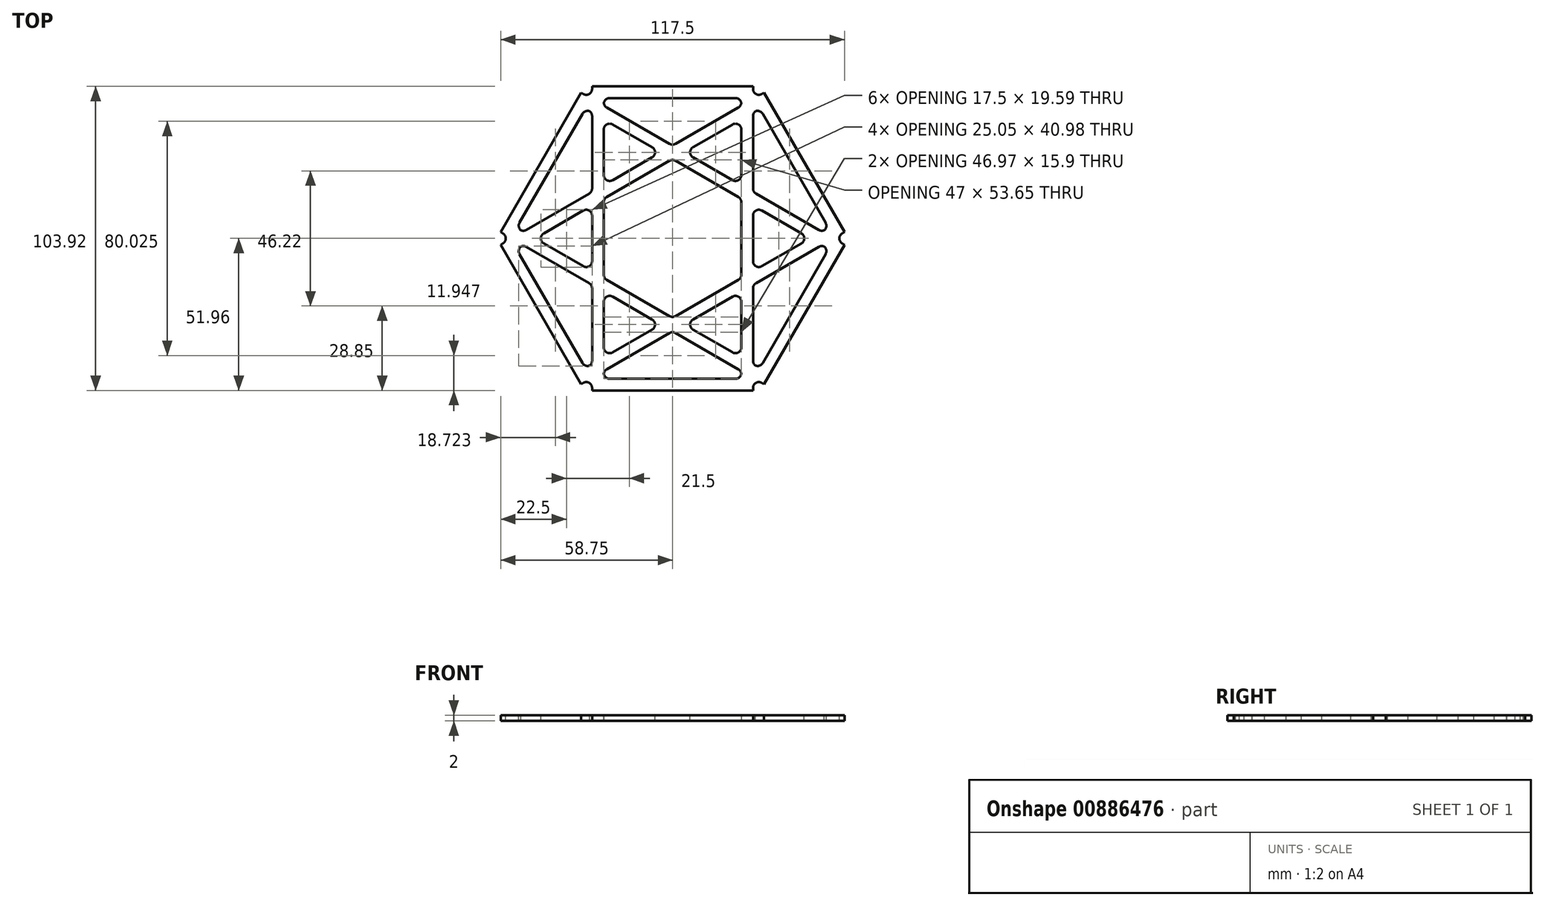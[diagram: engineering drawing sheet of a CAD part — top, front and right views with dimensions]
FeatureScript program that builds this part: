
annotation { "Feature Type Name" : "Feature", "Feature Type Description" : "" }
export const myFeature = defineFeature(function(context is Context, id is Id, definition is map)
    precondition{}
    {
        {
            var Q0;
            Q0=qCreatedBy(makeId("Top.planeOp"),FACE);
            var sketch = newSketch(context, id + "F0", { "sketchPlane" : qUnion([Q0])});
            skCircle(sketch, "E0.cCircle", {"center": v(0, 0) * mm, "radius": 60 * mm, "construction": true});
            skLineSegment(sketch, "E0.0", {"start": v(-60, 0) * mm, "end": v(-30, 51.96) * mm, "construction": true});
            skLineSegment(sketch, "E0.1", {"start": v(-30, 51.96) * mm, "end": v(30, 51.96) * mm, "construction": true});
            skLineSegment(sketch, "E0.2", {"start": v(30, 51.96) * mm, "end": v(60, 0) * mm, "construction": true});
            skLineSegment(sketch, "E0.3", {"start": v(60, 0) * mm, "end": v(30, -51.96) * mm, "construction": true});
            skLineSegment(sketch, "E0.4", {"start": v(30, -51.96) * mm, "end": v(-30, -51.96) * mm, "construction": true});
            skLineSegment(sketch, "E0.5", {"start": v(-30, -51.96) * mm, "end": v(-60, 0) * mm, "construction": true});
            skLineSegment(sketch, "E1.bottom", {"start": v(-27.5, 51.96) * mm, "end": v(27.5, 51.96) * mm});
            skLineSegment(sketch, "E1.top", {"start": v(-27.5, -51.96) * mm, "end": v(27.5, -51.96) * mm});
            skLineSegment(sketch, "E1.left", {"start": v(-27.5, 51.96) * mm, "end": v(-27.5, -51.96) * mm});
            skLineSegment(sketch, "E1.right", {"start": v(27.5, 51.96) * mm, "end": v(27.5, -51.96) * mm});
            skLineSegment(sketch, "E2.0", {"start": v(-23.5, -47.96) * mm, "end": v(23.5, -47.96) * mm});
            skLineSegment(sketch, "E2.1", {"start": v(-23.5, 47.96) * mm, "end": v(-23.5, -47.96) * mm});
            skLineSegment(sketch, "E2.2", {"start": v(-23.5, 47.96) * mm, "end": v(23.5, 47.96) * mm});
            skLineSegment(sketch, "E2.3", {"start": v(23.5, 47.96) * mm, "end": v(23.5, -47.96) * mm});
            skLineSegment(sketch, "E3.1.0", {"start": v(-29.79, -44.33) * mm, "end": v(53.29, 3.63) * mm});
            skLineSegment(sketch, "E3.1.1", {"start": v(58.75, 2.17) * mm, "end": v(31.25, 49.8) * mm});
            skLineSegment(sketch, "E3.1.2", {"start": v(-31.25, -49.8) * mm, "end": v(-58.75, -2.17) * mm});
            skLineSegment(sketch, "E3.1.3", {"start": v(-29.79, -44.33) * mm, "end": v(-53.29, -3.63) * mm});
            skLineSegment(sketch, "E3.1.4", {"start": v(-53.29, -3.63) * mm, "end": v(29.79, 44.33) * mm});
            skLineSegment(sketch, "E3.1.5", {"start": v(-58.75, -2.17) * mm, "end": v(31.25, 49.8) * mm});
            skLineSegment(sketch, "E3.1.7", {"start": v(53.29, 3.63) * mm, "end": v(29.79, 44.33) * mm});
            skLineSegment(sketch, "E3.1.8", {"start": v(-31.25, -49.8) * mm, "end": v(58.75, 2.17) * mm});
            skLineSegment(sketch, "E3.2.0", {"start": v(53.29, -3.63) * mm, "end": v(-29.79, 44.33) * mm});
            skLineSegment(sketch, "E3.2.1", {"start": v(-31.25, 49.8) * mm, "end": v(-58.75, 2.17) * mm});
            skLineSegment(sketch, "E3.2.2", {"start": v(58.75, -2.17) * mm, "end": v(31.25, -49.8) * mm});
            skLineSegment(sketch, "E3.2.3", {"start": v(53.29, -3.63) * mm, "end": v(29.79, -44.33) * mm});
            skLineSegment(sketch, "E3.2.4", {"start": v(29.79, -44.33) * mm, "end": v(-53.29, 3.63) * mm});
            skLineSegment(sketch, "E3.2.5", {"start": v(31.25, -49.8) * mm, "end": v(-58.75, 2.17) * mm});
            skLineSegment(sketch, "E3.2.7", {"start": v(-29.79, 44.33) * mm, "end": v(-53.29, 3.63) * mm});
            skLineSegment(sketch, "E3.2.8", {"start": v(58.75, -2.17) * mm, "end": v(-31.25, 49.8) * mm});
            skSolve(sketch);
        }
        {
            var Q0;
            {var subQ0=sQuery(id+"F0.wireOp",EDGE,"E3.1.4");var subQ1=sQuery(id+"F0.wireOp",EDGE,"E1.left");var subQ2=makeQuery(id+"F0.imprint","INTERSECT",VERTEX,{"derivedFrom":[subQ1,subQ0]});Q0=makeQuery(id+"F0.imprint","IMPRINT",FACE,{"disambiguationData":[TD([[makeQuery(id+"F0.imprint","IMPRINT",EDGE,{"disambiguationData":[TD([[subQ2,-1.0]])],"derivedFrom":subQ1}),1.0]])]});}
            var Q1;
            {var subQ0=sQuery(id+"F0.wireOp",EDGE,"E3.2.4");var subQ1=sQuery(id+"F0.wireOp",EDGE,"E1.left");var subQ2=makeQuery(id+"F0.imprint","INTERSECT",VERTEX,{"derivedFrom":[subQ1,subQ0]});Q1=makeQuery(id+"F0.imprint","IMPRINT",FACE,{"disambiguationData":[TD([[makeQuery(id+"F0.imprint","IMPRINT",EDGE,{"disambiguationData":[TD([[subQ2,-1.0]])],"derivedFrom":subQ1}),1.0]])]});}
            var Q2;
            {var subQ0=sQuery(id+"F0.wireOp",EDGE,"E3.2.4");var subQ1=sQuery(id+"F0.wireOp",EDGE,"E2.1");var subQ2=makeQuery(id+"F0.imprint","INTERSECT",VERTEX,{"derivedFrom":[subQ1,subQ0]});Q2=makeQuery(id+"F0.imprint","IMPRINT",FACE,{"disambiguationData":[TD([[makeQuery(id+"F0.imprint","IMPRINT",EDGE,{"disambiguationData":[TD([[subQ2,-1.0]])],"derivedFrom":subQ1}),1.0]])]});}
            var Q3;
            {var subQ0=sQuery(id+"F0.wireOp",EDGE,"E3.2.4");var subQ1=sQuery(id+"F0.wireOp",EDGE,"E1.left");var subQ2=makeQuery(id+"F0.imprint","INTERSECT",VERTEX,{"derivedFrom":[subQ1,subQ0]});Q3=makeQuery(id+"F0.imprint","IMPRINT",FACE,{"disambiguationData":[TD([[makeQuery(id+"F0.imprint","IMPRINT",EDGE,{"disambiguationData":[TD([[subQ2,-1.0]])],"derivedFrom":subQ1}),-1.0]])]});}
            var Q4;
            {var subQ0=sQuery(id+"F0.wireOp",EDGE,"E3.2.5");var subQ1=sQuery(id+"F0.wireOp",EDGE,"E1.left");var subQ2=makeQuery(id+"F0.imprint","INTERSECT",VERTEX,{"derivedFrom":[subQ1,subQ0]});Q4=makeQuery(id+"F0.imprint","IMPRINT",FACE,{"disambiguationData":[TD([[makeQuery(id+"F0.imprint","IMPRINT",EDGE,{"disambiguationData":[TD([[subQ2,-1.0]])],"derivedFrom":subQ1}),1.0]])]});}
            var Q5;
            {var subQ0=sQuery(id+"F0.wireOp",EDGE,"E3.1.8");var subQ1=sQuery(id+"F0.wireOp",EDGE,"E1.left");var subQ2=makeQuery(id+"F0.imprint","INTERSECT",VERTEX,{"derivedFrom":[subQ1,subQ0]});Q5=makeQuery(id+"F0.imprint","IMPRINT",FACE,{"disambiguationData":[TD([[makeQuery(id+"F0.imprint","IMPRINT",EDGE,{"disambiguationData":[TD([[subQ2,1.0]])],"derivedFrom":subQ1}),1.0]])]});}
            var Q6;
            {var subQ4=sQuery(id+"F0.wireOp",EDGE,"E3.1.2");Q6=makeQuery(id+"F0.imprint","IMPRINT",FACE,{"disambiguationData":[TD([[makeQuery(id+"F0.imprint","IMPRINT",EDGE,{"derivedFrom":subQ4}),-1.0]])]});}
            var Q7;
            {var subQ1=sQuery(id+"F0.wireOp",EDGE,"E1.top");Q7=makeQuery(id+"F0.imprint","IMPRINT",FACE,{"disambiguationData":[TD([[makeQuery(id+"F0.imprint","IMPRINT",EDGE,{"derivedFrom":subQ1}),1.0]])]});}
            var Q8;
            {var subQ0=sQuery(id+"F0.wireOp",EDGE,"E3.2.4");var subQ1=sQuery(id+"F0.wireOp",EDGE,"E2.3");var subQ2=makeQuery(id+"F0.imprint","INTERSECT",VERTEX,{"derivedFrom":[subQ1,subQ0]});Q8=makeQuery(id+"F0.imprint","IMPRINT",FACE,{"disambiguationData":[TD([[makeQuery(id+"F0.imprint","IMPRINT",EDGE,{"disambiguationData":[TD([[subQ2,-1.0]])],"derivedFrom":subQ1}),-1.0]])]});}
            var Q9;
            {var subQ0=sQuery(id+"F0.wireOp",EDGE,"E3.2.5");var subQ1=sQuery(id+"F0.wireOp",EDGE,"E1.right");var subQ2=makeQuery(id+"F0.imprint","INTERSECT",VERTEX,{"derivedFrom":[subQ1,subQ0]});Q9=makeQuery(id+"F0.imprint","IMPRINT",FACE,{"disambiguationData":[TD([[makeQuery(id+"F0.imprint","IMPRINT",EDGE,{"disambiguationData":[TD([[subQ2,1.0]])],"derivedFrom":subQ1}),-1.0]])]});}
            var Q10;
            {var subQ0=sQuery(id+"F0.wireOp",EDGE,"E3.2.5");var subQ1=sQuery(id+"F0.wireOp",EDGE,"E3.1.0");var subQ2=makeQuery(id+"F0.imprint","INTERSECT",VERTEX,{"derivedFrom":[subQ1,subQ0]});Q10=makeQuery(id+"F0.imprint","IMPRINT",FACE,{"disambiguationData":[TD([[makeQuery(id+"F0.imprint","IMPRINT",EDGE,{"disambiguationData":[TD([[subQ2,-1.0]])],"derivedFrom":subQ1}),-1.0]])]});}
            var Q11;
            {var subQ0=sQuery(id+"F0.wireOp",EDGE,"E3.1.0");var subQ1=sQuery(id+"F0.wireOp",EDGE,"E2.1");var subQ2=makeQuery(id+"F0.imprint","INTERSECT",VERTEX,{"derivedFrom":[subQ1,subQ0]});Q11=makeQuery(id+"F0.imprint","IMPRINT",FACE,{"disambiguationData":[TD([[makeQuery(id+"F0.imprint","IMPRINT",EDGE,{"disambiguationData":[TD([[subQ2,-1.0]])],"derivedFrom":subQ1}),1.0]])]});}
            var Q12;
            {var subQ0=sQuery(id+"F0.wireOp",EDGE,"E3.1.0");var subQ1=sQuery(id+"F0.wireOp",EDGE,"E2.3");var subQ2=makeQuery(id+"F0.imprint","INTERSECT",VERTEX,{"derivedFrom":[subQ1,subQ0]});Q12=makeQuery(id+"F0.imprint","IMPRINT",FACE,{"disambiguationData":[TD([[makeQuery(id+"F0.imprint","IMPRINT",EDGE,{"disambiguationData":[TD([[subQ2,-1.0]])],"derivedFrom":subQ1}),-1.0]])]});}
            var Q13;
            {var subQ0=sQuery(id+"F0.wireOp",EDGE,"E3.1.8");var subQ1=sQuery(id+"F0.wireOp",EDGE,"E1.right");var subQ2=makeQuery(id+"F0.imprint","INTERSECT",VERTEX,{"derivedFrom":[subQ1,subQ0]});Q13=makeQuery(id+"F0.imprint","IMPRINT",FACE,{"disambiguationData":[TD([[makeQuery(id+"F0.imprint","IMPRINT",EDGE,{"disambiguationData":[TD([[subQ2,-1.0]])],"derivedFrom":subQ1}),-1.0]])]});}
            var Q14;
            {var subQ0=sQuery(id+"F0.wireOp",EDGE,"E3.1.0");var subQ1=sQuery(id+"F0.wireOp",EDGE,"E1.right");var subQ2=makeQuery(id+"F0.imprint","INTERSECT",VERTEX,{"derivedFrom":[subQ1,subQ0]});Q14=makeQuery(id+"F0.imprint","IMPRINT",FACE,{"disambiguationData":[TD([[makeQuery(id+"F0.imprint","IMPRINT",EDGE,{"disambiguationData":[TD([[subQ2,-1.0]])],"derivedFrom":subQ1}),-1.0]])]});}
            var Q15;
            {var subQ0=sQuery(id+"F0.wireOp",EDGE,"E3.2.2");Q15=makeQuery(id+"F0.imprint","IMPRINT",FACE,{"disambiguationData":[TD([[makeQuery(id+"F0.imprint","IMPRINT",EDGE,{"derivedFrom":subQ0}),-1.0]])]});}
            var Q16;
            {var subQ0=sQuery(id+"F0.wireOp",EDGE,"E3.1.0");var subQ1=sQuery(id+"F0.wireOp",EDGE,"E1.right");var subQ2=makeQuery(id+"F0.imprint","INTERSECT",VERTEX,{"derivedFrom":[subQ1,subQ0]});Q16=makeQuery(id+"F0.imprint","IMPRINT",FACE,{"disambiguationData":[TD([[makeQuery(id+"F0.imprint","IMPRINT",EDGE,{"disambiguationData":[TD([[subQ2,-1.0]])],"derivedFrom":subQ1}),1.0]])]});}
            var Q17;
            {var subQ0=sQuery(id+"F0.wireOp",EDGE,"E3.2.5");var subQ1=sQuery(id+"F0.wireOp",EDGE,"E3.1.4");var subQ2=makeQuery(id+"F0.imprint","INTERSECT",VERTEX,{"derivedFrom":[subQ1,subQ0]});Q17=makeQuery(id+"F0.imprint","IMPRINT",FACE,{"disambiguationData":[TD([[makeQuery(id+"F0.imprint","IMPRINT",EDGE,{"disambiguationData":[TD([[subQ2,-1.0]])],"derivedFrom":subQ1}),1.0]])]});}
            var Q18;
            {var subQ0=sQuery(id+"F0.wireOp",EDGE,"E3.1.5");var subQ1=sQuery(id+"F0.wireOp",EDGE,"E1.left");var subQ2=makeQuery(id+"F0.imprint","INTERSECT",VERTEX,{"derivedFrom":[subQ1,subQ0]});Q18=makeQuery(id+"F0.imprint","IMPRINT",FACE,{"disambiguationData":[TD([[makeQuery(id+"F0.imprint","IMPRINT",EDGE,{"disambiguationData":[TD([[subQ2,-1.0]])],"derivedFrom":subQ1}),-1.0]])]});}
            var Q19;
            {var subQ0=sQuery(id+"F0.wireOp",EDGE,"E3.2.1");Q19=makeQuery(id+"F0.imprint","IMPRINT",FACE,{"disambiguationData":[TD([[makeQuery(id+"F0.imprint","IMPRINT",EDGE,{"derivedFrom":subQ0}),1.0]])]});}
            var Q20;
            {var subQ0=sQuery(id+"F0.wireOp",EDGE,"E3.2.0");var subQ1=sQuery(id+"F0.wireOp",EDGE,"E1.left");var subQ2=makeQuery(id+"F0.imprint","INTERSECT",VERTEX,{"derivedFrom":[subQ1,subQ0]});Q20=makeQuery(id+"F0.imprint","IMPRINT",FACE,{"disambiguationData":[TD([[makeQuery(id+"F0.imprint","IMPRINT",EDGE,{"disambiguationData":[TD([[subQ2,-1.0]])],"derivedFrom":subQ1}),1.0]])]});}
            var Q21;
            {var subQ0=sQuery(id+"F0.wireOp",EDGE,"E3.1.5");var subQ1=sQuery(id+"F0.wireOp",EDGE,"E2.1");var subQ2=makeQuery(id+"F0.imprint","INTERSECT",VERTEX,{"derivedFrom":[subQ1,subQ0]});Q21=makeQuery(id+"F0.imprint","IMPRINT",FACE,{"disambiguationData":[TD([[makeQuery(id+"F0.imprint","IMPRINT",EDGE,{"disambiguationData":[TD([[subQ2,-1.0]])],"derivedFrom":subQ1}),1.0]])]});}
            var Q22;
            {var subQ0=sQuery(id+"F0.wireOp",EDGE,"E3.1.5");var subQ1=sQuery(id+"F0.wireOp",EDGE,"E1.left");var subQ2=makeQuery(id+"F0.imprint","INTERSECT",VERTEX,{"derivedFrom":[subQ1,subQ0]});Q22=makeQuery(id+"F0.imprint","IMPRINT",FACE,{"disambiguationData":[TD([[makeQuery(id+"F0.imprint","IMPRINT",EDGE,{"disambiguationData":[TD([[subQ2,-1.0]])],"derivedFrom":subQ1}),1.0]])]});}
            var Q23;
            {var subQ0=sQuery(id+"F0.wireOp",EDGE,"E3.2.8");var subQ1=sQuery(id+"F0.wireOp",EDGE,"E2.1");var subQ2=makeQuery(id+"F0.imprint","INTERSECT",VERTEX,{"derivedFrom":[subQ1,subQ0]});Q23=makeQuery(id+"F0.imprint","IMPRINT",FACE,{"disambiguationData":[TD([[makeQuery(id+"F0.imprint","IMPRINT",EDGE,{"disambiguationData":[TD([[subQ2,-1.0]])],"derivedFrom":subQ1}),1.0]])]});}
            var Q24;
            {var subQ0=sQuery(id+"F0.wireOp",EDGE,"E3.2.8");var subQ1=sQuery(id+"F0.wireOp",EDGE,"E1.left");var subQ2=makeQuery(id+"F0.imprint","INTERSECT",VERTEX,{"derivedFrom":[subQ1,subQ0]});Q24=makeQuery(id+"F0.imprint","IMPRINT",FACE,{"disambiguationData":[TD([[makeQuery(id+"F0.imprint","IMPRINT",EDGE,{"disambiguationData":[TD([[subQ2,-1.0]])],"derivedFrom":subQ1}),1.0]])]});}
            var Q25;
            {var subQ5=sQuery(id+"F0.wireOp",EDGE,"E1.bottom");Q25=makeQuery(id+"F0.imprint","IMPRINT",FACE,{"disambiguationData":[TD([[makeQuery(id+"F0.imprint","IMPRINT",EDGE,{"derivedFrom":subQ5}),-1.0]])]});}
            var Q26;
            {var subQ0=sQuery(id+"F0.wireOp",EDGE,"E3.2.0");var subQ1=sQuery(id+"F0.wireOp",EDGE,"E3.1.4");var subQ2=makeQuery(id+"F0.imprint","INTERSECT",VERTEX,{"derivedFrom":[subQ1,subQ0]});Q26=makeQuery(id+"F0.imprint","IMPRINT",FACE,{"disambiguationData":[TD([[makeQuery(id+"F0.imprint","IMPRINT",EDGE,{"disambiguationData":[TD([[subQ2,-1.0]])],"derivedFrom":subQ1}),1.0]])]});}
            var Q27;
            {var subQ0=sQuery(id+"F0.wireOp",EDGE,"E3.1.5");var subQ1=sQuery(id+"F0.wireOp",EDGE,"E2.3");var subQ2=makeQuery(id+"F0.imprint","INTERSECT",VERTEX,{"derivedFrom":[subQ1,subQ0]});Q27=makeQuery(id+"F0.imprint","IMPRINT",FACE,{"disambiguationData":[TD([[makeQuery(id+"F0.imprint","IMPRINT",EDGE,{"disambiguationData":[TD([[subQ2,-1.0]])],"derivedFrom":subQ1}),-1.0]])]});}
            var Q28;
            {var subQ0=sQuery(id+"F0.wireOp",EDGE,"E3.2.8");var subQ1=sQuery(id+"F0.wireOp",EDGE,"E2.3");var subQ2=makeQuery(id+"F0.imprint","INTERSECT",VERTEX,{"derivedFrom":[subQ1,subQ0]});Q28=makeQuery(id+"F0.imprint","IMPRINT",FACE,{"disambiguationData":[TD([[makeQuery(id+"F0.imprint","IMPRINT",EDGE,{"disambiguationData":[TD([[subQ2,-1.0]])],"derivedFrom":subQ1}),-1.0]])]});}
            var Q29;
            {var subQ0=sQuery(id+"F0.wireOp",EDGE,"E3.1.4");var subQ1=sQuery(id+"F0.wireOp",EDGE,"E1.right");var subQ2=makeQuery(id+"F0.imprint","INTERSECT",VERTEX,{"derivedFrom":[subQ1,subQ0]});Q29=makeQuery(id+"F0.imprint","IMPRINT",FACE,{"disambiguationData":[TD([[makeQuery(id+"F0.imprint","IMPRINT",EDGE,{"disambiguationData":[TD([[subQ2,-1.0]])],"derivedFrom":subQ1}),-1.0]])]});}
            var Q30;
            {var subQ0=sQuery(id+"F0.wireOp",EDGE,"E3.1.5");var subQ1=sQuery(id+"F0.wireOp",EDGE,"E1.right");var subQ2=makeQuery(id+"F0.imprint","INTERSECT",VERTEX,{"derivedFrom":[subQ1,subQ0]});Q30=makeQuery(id+"F0.imprint","IMPRINT",FACE,{"disambiguationData":[TD([[makeQuery(id+"F0.imprint","IMPRINT",EDGE,{"disambiguationData":[TD([[subQ2,-1.0]])],"derivedFrom":subQ1}),-1.0]])]});}
            var Q31;
            {var subQ4=sQuery(id+"F0.wireOp",EDGE,"E3.1.1");Q31=makeQuery(id+"F0.imprint","IMPRINT",FACE,{"disambiguationData":[TD([[makeQuery(id+"F0.imprint","IMPRINT",EDGE,{"derivedFrom":subQ4}),1.0]])]});}
            var Q32;
            {var subQ0=sQuery(id+"F0.wireOp",EDGE,"E3.2.8");var subQ1=sQuery(id+"F0.wireOp",EDGE,"E1.right");var subQ2=makeQuery(id+"F0.imprint","INTERSECT",VERTEX,{"derivedFrom":[subQ1,subQ0]});Q32=makeQuery(id+"F0.imprint","IMPRINT",FACE,{"disambiguationData":[TD([[makeQuery(id+"F0.imprint","IMPRINT",EDGE,{"disambiguationData":[TD([[subQ2,-1.0]])],"derivedFrom":subQ1}),-1.0]])]});}
            var Q33;
            {var subQ0=sQuery(id+"F0.wireOp",EDGE,"E3.2.0");var subQ1=sQuery(id+"F0.wireOp",EDGE,"E1.right");var subQ2=makeQuery(id+"F0.imprint","INTERSECT",VERTEX,{"derivedFrom":[subQ1,subQ0]});Q33=makeQuery(id+"F0.imprint","IMPRINT",FACE,{"disambiguationData":[TD([[makeQuery(id+"F0.imprint","IMPRINT",EDGE,{"disambiguationData":[TD([[subQ2,-1.0]])],"derivedFrom":subQ1}),-1.0]])]});}
            var Q34;
            {var subQ0=sQuery(id+"F0.wireOp",EDGE,"E3.2.8");var subQ1=sQuery(id+"F0.wireOp",EDGE,"E1.right");var subQ2=makeQuery(id+"F0.imprint","INTERSECT",VERTEX,{"derivedFrom":[subQ1,subQ0]});Q34=makeQuery(id+"F0.imprint","IMPRINT",FACE,{"disambiguationData":[TD([[makeQuery(id+"F0.imprint","IMPRINT",EDGE,{"disambiguationData":[TD([[subQ2,-1.0]])],"derivedFrom":subQ1}),1.0]])]});}
            var Q35;
            {var subQ0=sQuery(id+"F0.wireOp",EDGE,"E3.2.0");var subQ1=sQuery(id+"F0.wireOp",EDGE,"E3.1.0");var subQ2=makeQuery(id+"F0.imprint","INTERSECT",VERTEX,{"derivedFrom":[subQ1,subQ0]});Q35=makeQuery(id+"F0.imprint","IMPRINT",FACE,{"disambiguationData":[TD([[makeQuery(id+"F0.imprint","IMPRINT",EDGE,{"disambiguationData":[TD([[subQ2,-1.0]])],"derivedFrom":subQ1}),-1.0]])]});}
            extrude(context, id + "F1", {"entities" : qUnion([Q0, Q1, Q2, Q3, Q4, Q5, Q6, Q7, Q8, Q9, Q10, Q11, Q12, Q13, Q14, Q15, Q16, Q17, Q18, Q19, Q20, Q21, Q22, Q23, Q24, Q25, Q26, Q27, Q28, Q29, Q30, Q31, Q32, Q33, Q34, Q35]), "depth" : 2 * mm, "offsetDistance" : 25 * mm});
        }
        {
            var Q0;
            Q0=makeQuery(id+"F1.opExtrude","SWEPT_EDGE",EDGE,{"disambiguationData":[OSD([sQuery(id+"F0.wireOp",EDGE,"E2.1"),sQuery(id+"F0.wireOp",EDGE,"E2.2")])]});
            var Q1;
            Q1=makeQuery(id+"F1.opExtrude","SWEPT_EDGE",EDGE,{"disambiguationData":[OSD([sQuery(id+"F0.wireOp",EDGE,"E3.2.0"),sQuery(id+"F0.wireOp",EDGE,"E3.2.7")])]});
            var Q2;
            Q2=makeQuery(id+"F1.opExtrude","SWEPT_EDGE",EDGE,{"disambiguationData":[OSD([sQuery(id+"F0.wireOp",EDGE,"E2.1"),sQuery(id+"F0.wireOp",EDGE,"E3.2.0")])]});
            var Q3;
            Q3=makeQuery(id+"F1.opExtrude","SWEPT_EDGE",EDGE,{"disambiguationData":[OSD([sQuery(id+"F0.wireOp",EDGE,"E2.1"),sQuery(id+"F0.wireOp",EDGE,"E3.1.4")])]});
            var Q4;
            Q4=makeQuery(id+"F1.opExtrude","SWEPT_EDGE",EDGE,{"disambiguationData":[OSD([sQuery(id+"F0.wireOp",EDGE,"E3.1.4"),sQuery(id+"F0.wireOp",EDGE,"E3.2.0")])]});
            var Q5;
            Q5=makeQuery(id+"F1.opExtrude","SWEPT_EDGE",EDGE,{"disambiguationData":[OSD([sQuery(id+"F0.wireOp",EDGE,"E2.2"),sQuery(id+"F0.wireOp",EDGE,"E2.3")])]});
            var Q6;
            Q6=makeQuery(id+"F1.opExtrude","SWEPT_EDGE",EDGE,{"disambiguationData":[OSD([sQuery(id+"F0.wireOp",EDGE,"E2.3"),sQuery(id+"F0.wireOp",EDGE,"E3.1.4")])]});
            var Q7;
            Q7=makeQuery(id+"F1.opExtrude","SWEPT_EDGE",EDGE,{"disambiguationData":[OSD([sQuery(id+"F0.wireOp",EDGE,"E3.1.4"),sQuery(id+"F0.wireOp",EDGE,"E3.1.7")])]});
            var Q8;
            Q8=makeQuery(id+"F1.opExtrude","SWEPT_EDGE",EDGE,{"disambiguationData":[OSD([sQuery(id+"F0.wireOp",EDGE,"E2.3"),sQuery(id+"F0.wireOp",EDGE,"E3.2.0")])]});
            var Q9;
            Q9=makeQuery(id+"F1.opExtrude","SWEPT_EDGE",EDGE,{"disambiguationData":[OSD([sQuery(id+"F0.wireOp",EDGE,"E1.left"),sQuery(id+"F0.wireOp",EDGE,"E3.1.4")])]});
            var Q10;
            Q10=makeQuery(id+"F1.opExtrude","SWEPT_EDGE",EDGE,{"disambiguationData":[OSD([sQuery(id+"F0.wireOp",EDGE,"E1.left"),sQuery(id+"F0.wireOp",EDGE,"E3.2.5")])]});
            var Q11;
            Q11=makeQuery(id+"F1.opExtrude","SWEPT_EDGE",EDGE,{"disambiguationData":[OSD([sQuery(id+"F0.wireOp",EDGE,"E3.1.3"),sQuery(id+"F0.wireOp",EDGE,"E3.1.4")])]});
            var Q12;
            Q12=makeQuery(id+"F1.opExtrude","SWEPT_EDGE",EDGE,{"disambiguationData":[OSD([sQuery(id+"F0.wireOp",EDGE,"E3.1.4"),sQuery(id+"F0.wireOp",EDGE,"E3.2.4")])]});
            var Q13;
            Q13=makeQuery(id+"F1.opExtrude","SWEPT_EDGE",EDGE,{"disambiguationData":[OSD([sQuery(id+"F0.wireOp",EDGE,"E3.2.4"),sQuery(id+"F0.wireOp",EDGE,"E3.2.7")])]});
            var Q14;
            Q14=makeQuery(id+"F1.opExtrude","SWEPT_EDGE",EDGE,{"disambiguationData":[OSD([sQuery(id+"F0.wireOp",EDGE,"E2.1"),sQuery(id+"F0.wireOp",EDGE,"E3.2.4")])]});
            var Q15;
            Q15=makeQuery(id+"F1.opExtrude","SWEPT_EDGE",EDGE,{"disambiguationData":[OSD([sQuery(id+"F0.wireOp",EDGE,"E3.1.0"),sQuery(id+"F0.wireOp",EDGE,"E3.1.3")])]});
            var Q16;
            Q16=makeQuery(id+"F1.opExtrude","SWEPT_EDGE",EDGE,{"disambiguationData":[OSD([sQuery(id+"F0.wireOp",EDGE,"E2.1"),sQuery(id+"F0.wireOp",EDGE,"E3.1.0")])]});
            var Q17;
            Q17=makeQuery(id+"F1.opExtrude","SWEPT_EDGE",EDGE,{"disambiguationData":[OSD([sQuery(id+"F0.wireOp",EDGE,"E2.0"),sQuery(id+"F0.wireOp",EDGE,"E2.1")])]});
            var Q18;
            Q18=makeQuery(id+"F1.opExtrude","SWEPT_EDGE",EDGE,{"disambiguationData":[OSD([sQuery(id+"F0.wireOp",EDGE,"E3.1.0"),sQuery(id+"F0.wireOp",EDGE,"E3.2.4")])]});
            var Q19;
            Q19=makeQuery(id+"F1.opExtrude","SWEPT_EDGE",EDGE,{"disambiguationData":[OSD([sQuery(id+"F0.wireOp",EDGE,"E1.right"),sQuery(id+"F0.wireOp",EDGE,"E3.2.0")])]});
            var Q20;
            Q20=makeQuery(id+"F1.opExtrude","SWEPT_EDGE",EDGE,{"disambiguationData":[OSD([sQuery(id+"F0.wireOp",EDGE,"E1.right"),sQuery(id+"F0.wireOp",EDGE,"E3.1.8")])]});
            var Q21;
            Q21=makeQuery(id+"F1.opExtrude","SWEPT_EDGE",EDGE,{"disambiguationData":[OSD([sQuery(id+"F0.wireOp",EDGE,"E3.1.8"),sQuery(id+"F0.wireOp",EDGE,"E3.2.0")])]});
            var Q22;
            Q22=makeQuery(id+"F1.opExtrude","SWEPT_EDGE",EDGE,{"disambiguationData":[OSD([sQuery(id+"F0.wireOp",EDGE,"E3.2.0"),sQuery(id+"F0.wireOp",EDGE,"E3.2.3")])]});
            var Q23;
            Q23=makeQuery(id+"F1.opExtrude","SWEPT_EDGE",EDGE,{"disambiguationData":[OSD([sQuery(id+"F0.wireOp",EDGE,"E3.1.0"),sQuery(id+"F0.wireOp",EDGE,"E3.1.7")])]});
            var Q24;
            Q24=makeQuery(id+"F1.opExtrude","SWEPT_EDGE",EDGE,{"disambiguationData":[OSD([sQuery(id+"F0.wireOp",EDGE,"E3.1.0"),sQuery(id+"F0.wireOp",EDGE,"E3.2.0")])]});
            var Q25;
            Q25=makeQuery(id+"F1.opExtrude","SWEPT_EDGE",EDGE,{"disambiguationData":[OSD([sQuery(id+"F0.wireOp",EDGE,"E1.right"),sQuery(id+"F0.wireOp",EDGE,"E3.1.4")])]});
            var Q26;
            Q26=makeQuery(id+"F1.opExtrude","SWEPT_EDGE",EDGE,{"disambiguationData":[OSD([sQuery(id+"F0.wireOp",EDGE,"E2.3"),sQuery(id+"F0.wireOp",EDGE,"E3.1.5")])]});
            var Q27;
            Q27=makeQuery(id+"F1.opExtrude","SWEPT_EDGE",EDGE,{"disambiguationData":[OSD([sQuery(id+"F0.wireOp",EDGE,"E2.1"),sQuery(id+"F0.wireOp",EDGE,"E3.2.8")])]});
            var Q28;
            Q28=makeQuery(id+"F1.opExtrude","SWEPT_EDGE",EDGE,{"disambiguationData":[OSD([sQuery(id+"F0.wireOp",EDGE,"E3.1.5"),sQuery(id+"F0.wireOp",EDGE,"E3.2.4")])]});
            var Q29;
            Q29=makeQuery(id+"F1.opExtrude","SWEPT_EDGE",EDGE,{"disambiguationData":[OSD([sQuery(id+"F0.wireOp",EDGE,"E2.1"),sQuery(id+"F0.wireOp",EDGE,"E3.1.5")])]});
            var Q30;
            Q30=makeQuery(id+"F1.opExtrude","SWEPT_EDGE",EDGE,{"disambiguationData":[OSD([sQuery(id+"F0.wireOp",EDGE,"E3.1.5"),sQuery(id+"F0.wireOp",EDGE,"E3.2.8")])]});
            var Q31;
            Q31=makeQuery(id+"F1.opExtrude","SWEPT_EDGE",EDGE,{"disambiguationData":[OSD([sQuery(id+"F0.wireOp",EDGE,"E1.left"),sQuery(id+"F0.wireOp",EDGE,"E3.1.5")])]});
            var Q32;
            Q32=makeQuery(id+"F1.opExtrude","SWEPT_EDGE",EDGE,{"disambiguationData":[OSD([sQuery(id+"F0.wireOp",EDGE,"E3.1.5"),sQuery(id+"F0.wireOp",EDGE,"E3.2.0")])]});
            var Q33;
            Q33=makeQuery(id+"F1.opExtrude","SWEPT_EDGE",EDGE,{"disambiguationData":[OSD([sQuery(id+"F0.wireOp",EDGE,"E2.3"),sQuery(id+"F0.wireOp",EDGE,"E3.1.0")])]});
            var Q34;
            Q34=makeQuery(id+"F1.opExtrude","SWEPT_EDGE",EDGE,{"disambiguationData":[OSD([sQuery(id+"F0.wireOp",EDGE,"E2.3"),sQuery(id+"F0.wireOp",EDGE,"E3.2.8")])]});
            var Q35;
            Q35=makeQuery(id+"F1.opExtrude","SWEPT_EDGE",EDGE,{"disambiguationData":[OSD([sQuery(id+"F0.wireOp",EDGE,"E2.3"),sQuery(id+"F0.wireOp",EDGE,"E3.2.4")])]});
            var Q36;
            Q36=makeQuery(id+"F1.opExtrude","SWEPT_EDGE",EDGE,{"disambiguationData":[OSD([sQuery(id+"F0.wireOp",EDGE,"E2.0"),sQuery(id+"F0.wireOp",EDGE,"E2.3")])]});
            var Q37;
            Q37=makeQuery(id+"F1.opExtrude","SWEPT_EDGE",EDGE,{"disambiguationData":[OSD([sQuery(id+"F0.wireOp",EDGE,"E3.2.3"),sQuery(id+"F0.wireOp",EDGE,"E3.2.4")])]});
            var Q38;
            Q38=makeQuery(id+"F1.opExtrude","SWEPT_EDGE",EDGE,{"disambiguationData":[OSD([sQuery(id+"F0.wireOp",EDGE,"E2.1"),sQuery(id+"F0.wireOp",EDGE,"E3.2.5")])]});
            var Q39;
            Q39=makeQuery(id+"F1.opExtrude","SWEPT_EDGE",EDGE,{"disambiguationData":[OSD([sQuery(id+"F0.wireOp",EDGE,"E3.1.8"),sQuery(id+"F0.wireOp",EDGE,"E3.2.5")])]});
            var Q40;
            Q40=makeQuery(id+"F1.opExtrude","SWEPT_EDGE",EDGE,{"disambiguationData":[OSD([sQuery(id+"F0.wireOp",EDGE,"E3.1.0"),sQuery(id+"F0.wireOp",EDGE,"E3.2.5")])]});
            var Q41;
            Q41=makeQuery(id+"F1.opExtrude","SWEPT_EDGE",EDGE,{"disambiguationData":[OSD([sQuery(id+"F0.wireOp",EDGE,"E1.left"),sQuery(id+"F0.wireOp",EDGE,"E3.1.0")])]});
            var Q42;
            Q42=makeQuery(id+"F1.opExtrude","SWEPT_EDGE",EDGE,{"disambiguationData":[OSD([sQuery(id+"F0.wireOp",EDGE,"E1.left"),sQuery(id+"F0.wireOp",EDGE,"E3.2.4")])]});
            var Q43;
            Q43=makeQuery(id+"F1.opExtrude","SWEPT_EDGE",EDGE,{"disambiguationData":[OSD([sQuery(id+"F0.wireOp",EDGE,"E1.left"),sQuery(id+"F0.wireOp",EDGE,"E3.2.0")])]});
            var Q44;
            Q44=makeQuery(id+"F1.opExtrude","SWEPT_EDGE",EDGE,{"disambiguationData":[OSD([sQuery(id+"F0.wireOp",EDGE,"E1.right"),sQuery(id+"F0.wireOp",EDGE,"E3.2.8")])]});
            var Q45;
            Q45=makeQuery(id+"F1.opExtrude","SWEPT_EDGE",EDGE,{"disambiguationData":[OSD([sQuery(id+"F0.wireOp",EDGE,"E3.1.0"),sQuery(id+"F0.wireOp",EDGE,"E3.2.8")])]});
            var Q46;
            Q46=makeQuery(id+"F1.opExtrude","SWEPT_EDGE",EDGE,{"disambiguationData":[OSD([sQuery(id+"F0.wireOp",EDGE,"E1.right"),sQuery(id+"F0.wireOp",EDGE,"E3.2.4")])]});
            var Q47;
            Q47=makeQuery(id+"F1.opExtrude","SWEPT_EDGE",EDGE,{"disambiguationData":[OSD([sQuery(id+"F0.wireOp",EDGE,"E2.3"),sQuery(id+"F0.wireOp",EDGE,"E3.2.5")])]});
            var Q48;
            Q48=makeQuery(id+"F1.opExtrude","SWEPT_EDGE",EDGE,{"disambiguationData":[OSD([sQuery(id+"F0.wireOp",EDGE,"E2.1"),sQuery(id+"F0.wireOp",EDGE,"E3.1.8")])]});
            var Q49;
            Q49=makeQuery(id+"F1.opExtrude","SWEPT_EDGE",EDGE,{"disambiguationData":[OSD([sQuery(id+"F0.wireOp",EDGE,"E1.left"),sQuery(id+"F0.wireOp",EDGE,"E3.1.8")])]});
            var Q50;
            Q50=makeQuery(id+"F1.opExtrude","SWEPT_EDGE",EDGE,{"disambiguationData":[OSD([sQuery(id+"F0.wireOp",EDGE,"E1.right"),sQuery(id+"F0.wireOp",EDGE,"E3.2.5")])]});
            var Q51;
            Q51=makeQuery(id+"F1.opExtrude","SWEPT_EDGE",EDGE,{"disambiguationData":[OSD([sQuery(id+"F0.wireOp",EDGE,"E3.1.8"),sQuery(id+"F0.wireOp",EDGE,"E3.2.8")])]});
            var Q52;
            Q52=makeQuery(id+"F1.opExtrude","SWEPT_EDGE",EDGE,{"disambiguationData":[OSD([sQuery(id+"F0.wireOp",EDGE,"E1.right"),sQuery(id+"F0.wireOp",EDGE,"E3.1.5")])]});
            var Q53;
            Q53=makeQuery(id+"F1.opExtrude","SWEPT_EDGE",EDGE,{"disambiguationData":[OSD([sQuery(id+"F0.wireOp",EDGE,"E1.left"),sQuery(id+"F0.wireOp",EDGE,"E3.2.8")])]});
            var Q54;
            Q54=makeQuery(id+"F1.opExtrude","SWEPT_EDGE",EDGE,{"disambiguationData":[OSD([sQuery(id+"F0.wireOp",EDGE,"E3.1.5"),sQuery(id+"F0.wireOp",EDGE,"E3.2.5")])]});
            var Q55;
            Q55=makeQuery(id+"F1.opExtrude","SWEPT_EDGE",EDGE,{"disambiguationData":[OSD([sQuery(id+"F0.wireOp",EDGE,"E2.3"),sQuery(id+"F0.wireOp",EDGE,"E3.1.8")])]});
            var Q56;
            Q56=makeQuery(id+"F1.opExtrude","SWEPT_EDGE",EDGE,{"disambiguationData":[OSD([sQuery(id+"F0.wireOp",EDGE,"E3.1.8"),sQuery(id+"F0.wireOp",EDGE,"E3.2.4")])]});
            var Q57;
            Q57=makeQuery(id+"F1.opExtrude","SWEPT_EDGE",EDGE,{"disambiguationData":[OSD([sQuery(id+"F0.wireOp",EDGE,"E1.right"),sQuery(id+"F0.wireOp",EDGE,"E3.1.0")])]});
            var Q58;
            Q58=makeQuery(id+"F1.opExtrude","SWEPT_EDGE",EDGE,{"disambiguationData":[OSD([sQuery(id+"F0.wireOp",EDGE,"E3.1.4"),sQuery(id+"F0.wireOp",EDGE,"E3.2.8")])]});
            var Q59;
            Q59=makeQuery(id+"F1.opExtrude","SWEPT_EDGE",EDGE,{"disambiguationData":[OSD([sQuery(id+"F0.wireOp",EDGE,"E3.1.4"),sQuery(id+"F0.wireOp",EDGE,"E3.2.5")])]});
            fillet(context, id + "F2", {"entities" : qUnion([Q0, Q1, Q2, Q3, Q4, Q5, Q6, Q7, Q8, Q9, Q10, Q11, Q12, Q13, Q14, Q15, Q16, Q17, Q18, Q19, Q20, Q21, Q22, Q23, Q24, Q25, Q26, Q27, Q28, Q29, Q30, Q31, Q32, Q33, Q34, Q35, Q36, Q37, Q38, Q39, Q40, Q41, Q42, Q43, Q44, Q45, Q46, Q47, Q48, Q49, Q50, Q51, Q52, Q53, Q54, Q55, Q56, Q57, Q58, Q59]), "radius" : 2 * mm, "tangentPropagation" : true, "allowEdgeOverflow" : false});
        }
    });
